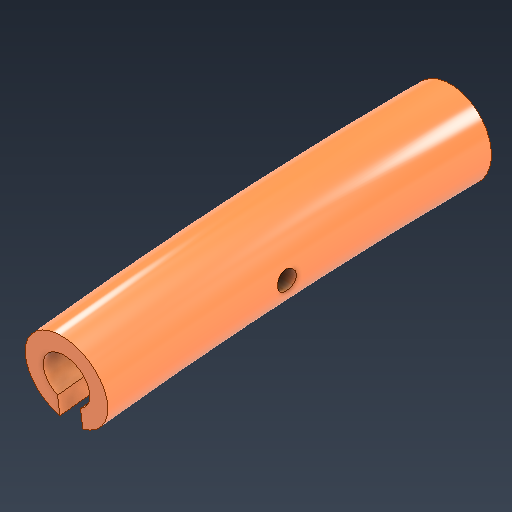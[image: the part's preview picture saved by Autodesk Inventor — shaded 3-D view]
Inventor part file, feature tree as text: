
AUTODESK INVENTOR PART (.ipt)
format: ipt  version: 2021 (Build 250183000, 183)  size: 221,184 bytes
history: native  units: mm
features: sketch x4, extrude x2, revolve x1
ambient origin geometry x8: Origin, YZ Plane, XZ Plane, XY Plane, X Axis, Y Axis, Z Axis, Center Point
bodies: Solid1 (feature_tree)
feature tree (7):
  sketch  "Sketch1"  dims[d0=3300.0mm d1=1650.0mm]
  revolve  "Revolution1"  [1 undecoded]
  extrude  "Extrusion1"  Depth=43.0mm
  extrude  "Extrusion2"  Depth=1.22173mm
  sketch  "Sketch2"  dims[d2=0.0mm d3=43.0mm]
  sketch  "Sketch3"  dims[d4=9.3mm d5=1.22173mm]
  sketch  "Sketch4"  dims[d6=12.0mm d7=0.0mm d8=3300.0mm d9=10.0mm d10=100.0mm d11=0.0mm]
note: 1 required parameter value undecoded (feature->parameter linkage not recoverable at this tier; creation-order binding heuristic only, values carry confidence <= 0.55)
